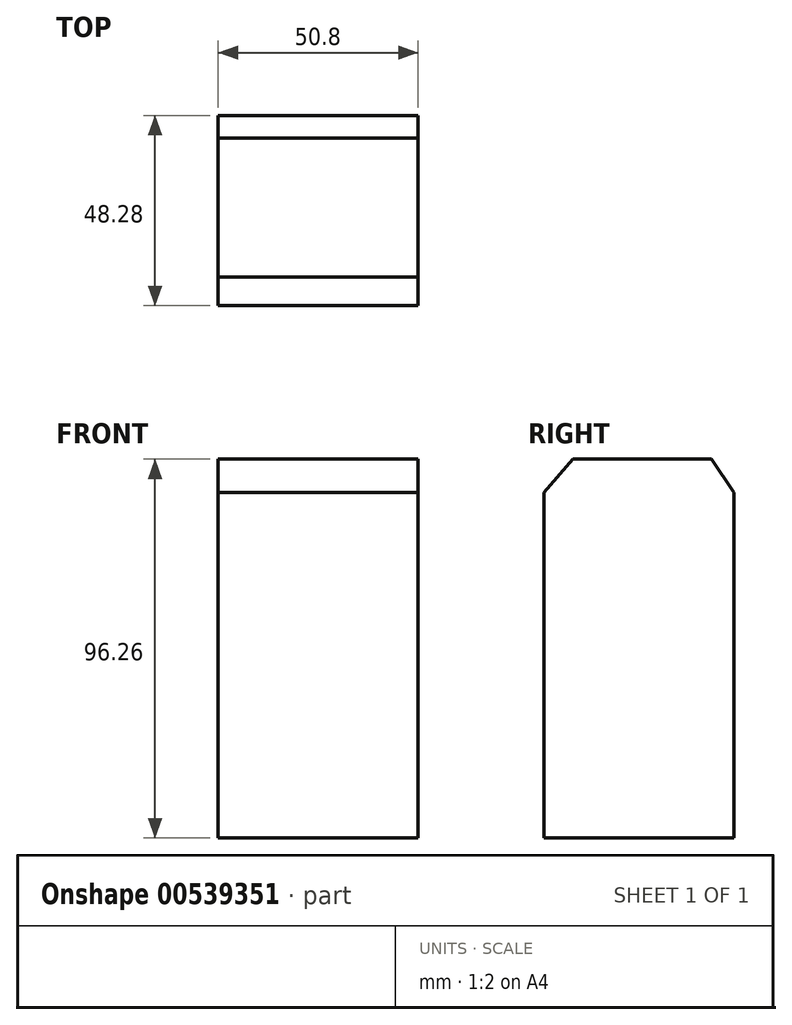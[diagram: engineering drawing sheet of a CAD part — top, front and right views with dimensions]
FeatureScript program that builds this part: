
annotation { "Feature Type Name" : "Feature", "Feature Type Description" : "" }
export const myFeature = defineFeature(function(context is Context, id is Id, definition is map)
    precondition{}
    {
        {
            var Q0;
            Q0=qCreatedBy(makeId("Right.planeOp"),FACE);
            var sketch = newSketch(context, id + "F0", { "sketchPlane" : qUnion([Q0])});
            skLineSegment(sketch, "E0.bottom", {"start": v(-25.5, 39.63) * mm, "end": v(22.77, 39.63) * mm});
            skLineSegment(sketch, "E0.top", {"start": v(-25.5, -48.13) * mm, "end": v(22.77, -48.13) * mm});
            skLineSegment(sketch, "E0.left", {"start": v(-25.5, 39.63) * mm, "end": v(-25.5, -48.13) * mm});
            skLineSegment(sketch, "E0.right", {"start": v(22.77, 39.63) * mm, "end": v(22.77, -48.13) * mm});
            skLineSegment(sketch, "E1", {"start": v(-25.5, 39.63) * mm, "end": v(-18.22, 48.13) * mm});
            skLineSegment(sketch, "E2", {"start": v(-18.22, 48.13) * mm, "end": v(17, 48.13) * mm});
            skLineSegment(sketch, "E3", {"start": v(17, 48.13) * mm, "end": v(22.77, 39.63) * mm});
            skSolve(sketch);
        }
        {
            var Q0;
            Q0 = qSketchRegion(id + "F0", true);
            var Q1;
            Q1=makeQuery(id+"F0.imprint","IMPRINT",FACE,{"disambiguationData":[TD([[makeQuery(id+"F0.imprint","IMPRINT",EDGE,{"derivedFrom":sQuery(id+"F0.wireOp",EDGE,"E0.bottom")}),-1.0]])]});
            extrude(context, id + "F1", {"entities" : qUnion([Q0, Q1]), "depth" : 25.4 * mm, "offsetDistance" : 25.4 * mm, "hasSecondDirection" : true, "secondDirectionOppositeDirection" : true, "secondDirectionDepth" : 25.4 * mm});
        }
    });
